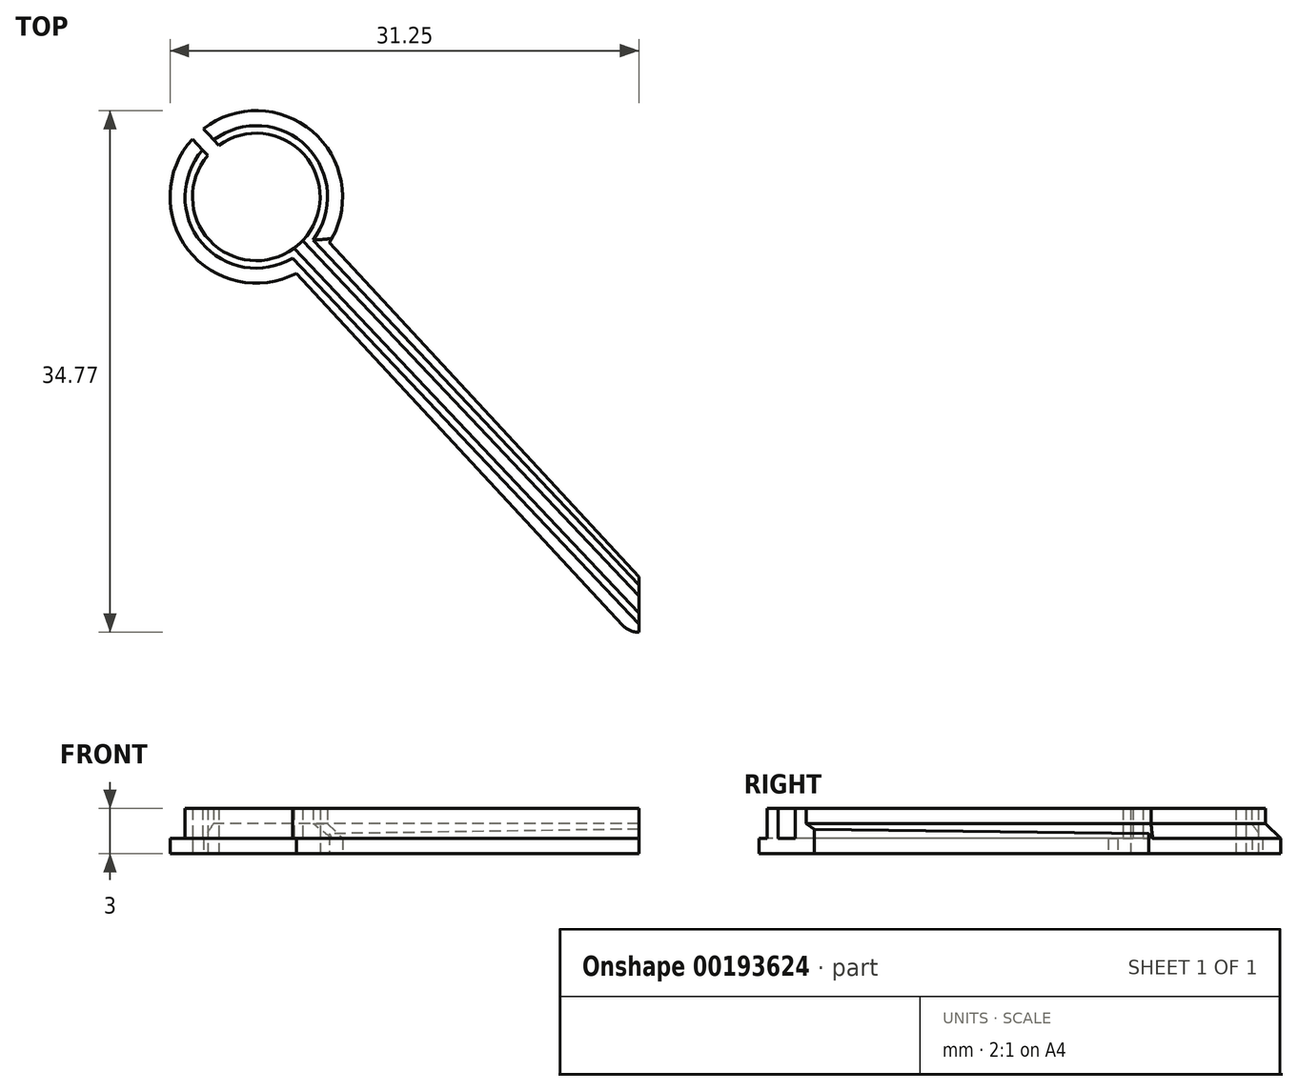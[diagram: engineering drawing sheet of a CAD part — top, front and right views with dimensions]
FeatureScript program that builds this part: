
annotation { "Feature Type Name" : "Feature", "Feature Type Description" : "" }
export const myFeature = defineFeature(function(context is Context, id is Id, definition is map)
    precondition{}
    {
        {
            var Q0;
            Q0=qCreatedBy(makeId("Top.planeOp"),FACE);
            var sketch = newSketch(context, id + "F0", { "sketchPlane" : qUnion([Q0])});
            skCircle(sketch, "E0", {"center": v(-37, 37) * mm, "radius": 4.25 * mm});
            skCircle(sketch, "E1", {"center": v(-9, 21) * mm, "radius": 1.7 * mm});
            skLineSegment(sketch, "E2", {"start": v(-51.17, 0) * mm, "end": v(69.36, 0) * mm, "construction": true});
            skLineSegment(sketch, "E3", {"start": v(0, -19.4) * mm, "end": v(0, 36.88) * mm, "construction": true});
            skCircle(sketch, "E4.MirrorC", {"center": v(37, 37) * mm, "radius": 4.25 * mm});
            skCircle(sketch, "E5.MirrorC", {"center": v(37, -37) * mm, "radius": 4.25 * mm});
            skCircle(sketch, "E6.MirrorC", {"center": v(-37, -37) * mm, "radius": 4.25 * mm});
            skCircle(sketch, "E7.MirrorC", {"center": v(-9, -21) * mm, "radius": 1.7 * mm});
            skCircle(sketch, "E8.MirrorC", {"center": v(9, -21) * mm, "radius": 1.7 * mm});
            skCircle(sketch, "E9.MirrorC", {"center": v(9, 21) * mm, "radius": 1.7 * mm});
            skCircle(sketch, "E10", {"center": v(-9, 21) * mm, "radius": 2.5 * mm});
            skCircle(sketch, "E11.MirrorC", {"center": v(9, 21) * mm, "radius": 2.5 * mm});
            skCircle(sketch, "E12.MirrorC", {"center": v(-9, -21) * mm, "radius": 2.5 * mm});
            skCircle(sketch, "E13.MirrorC", {"center": v(9, -21) * mm, "radius": 2.5 * mm});
            skCircle(sketch, "E14", {"center": v(-37, 37) * mm, "radius": 5.75 * mm});
            skCircle(sketch, "E15.MirrorC", {"center": v(37, 37) * mm, "radius": 5.75 * mm});
            skCircle(sketch, "E16.MirrorC", {"center": v(-37, -37) * mm, "radius": 5.75 * mm});
            skCircle(sketch, "E17.MirrorC", {"center": v(37, -37) * mm, "radius": 5.75 * mm});
            skLineSegment(sketch, "E18", {"start": v(-11.5, 18) * mm, "end": v(-8.5, 18) * mm});
            skLineSegment(sketch, "E19", {"start": v(-11.5, 15) * mm, "end": v(-11.5, 18) * mm});
            skPoint(sketch, "E20", {"position": v(0, 0) * mm});
            skLineSegment(sketch, "E21", {"start": v(-11.5, 15) * mm, "end": v(-8.5, 15) * mm});
            skLineSegment(sketch, "E22", {"start": v(-8.5, 15) * mm, "end": v(-8.5, 18) * mm});
            skLineSegment(sketch, "E23", {"start": v(-8.5, 17) * mm, "end": v(-10.5, 17) * mm});
            skLineSegment(sketch, "E24", {"start": v(-10.5, 17) * mm, "end": v(-10.5, 15) * mm});
            skLineSegment(sketch, "E25.MirrorCS", {"start": v(11.5, 18) * mm, "end": v(8.5, 18) * mm});
            skLineSegment(sketch, "E26.MirrorCS", {"start": v(8.5, 17) * mm, "end": v(10.5, 17) * mm});
            skLineSegment(sketch, "E27.MirrorCS", {"start": v(10.5, 17) * mm, "end": v(10.5, 15) * mm});
            skLineSegment(sketch, "E28.MirrorCS", {"start": v(11.5, 15) * mm, "end": v(8.5, 15) * mm});
            skLineSegment(sketch, "E29.MirrorCS", {"start": v(8.5, 15) * mm, "end": v(8.5, 18) * mm});
            skLineSegment(sketch, "E30.MirrorCS", {"start": v(11.5, 15) * mm, "end": v(11.5, 18) * mm});
            skLineSegment(sketch, "E31.MirrorCS", {"start": v(-8.5, -15) * mm, "end": v(-8.5, -18) * mm});
            skLineSegment(sketch, "E32.MirrorCS", {"start": v(-8.5, -17) * mm, "end": v(-10.5, -17) * mm});
            skLineSegment(sketch, "E33.MirrorCS", {"start": v(8.5, -17) * mm, "end": v(10.5, -17) * mm});
            skLineSegment(sketch, "E34.MirrorCS", {"start": v(8.5, -15) * mm, "end": v(8.5, -18) * mm});
            skLineSegment(sketch, "E35.MirrorCS", {"start": v(11.5, -15) * mm, "end": v(8.5, -15) * mm});
            skLineSegment(sketch, "E36.MirrorCS", {"start": v(-11.5, -15) * mm, "end": v(-8.5, -15) * mm});
            skLineSegment(sketch, "E37.MirrorCS", {"start": v(10.5, -17) * mm, "end": v(10.5, -15) * mm});
            skLineSegment(sketch, "E38.MirrorCS", {"start": v(-10.5, -17) * mm, "end": v(-10.5, -15) * mm});
            skLineSegment(sketch, "E39.MirrorCS", {"start": v(-11.5, -15) * mm, "end": v(-11.5, -18) * mm});
            skLineSegment(sketch, "E40.MirrorCS", {"start": v(11.5, -18) * mm, "end": v(8.5, -18) * mm});
            skLineSegment(sketch, "E41.MirrorCS", {"start": v(-11.5, -18) * mm, "end": v(-8.5, -18) * mm});
            skLineSegment(sketch, "E42.MirrorCS", {"start": v(11.5, -15) * mm, "end": v(11.5, -18) * mm});
            skLineSegment(sketch, "E43.bottom", {"start": v(-11.5, 23.5) * mm, "end": v(11.5, 23.5) * mm});
            skLineSegment(sketch, "E43.top", {"start": v(-11.5, -23.5) * mm, "end": v(11.5, -23.5) * mm});
            skLineSegment(sketch, "E43.left", {"start": v(-11.5, 23.5) * mm, "end": v(-11.5, -23.5) * mm});
            skLineSegment(sketch, "E43.right", {"start": v(11.5, 23.5) * mm, "end": v(11.5, -23.5) * mm});
            skLineSegment(sketch, "E44", {"start": v(-37, 37) * mm, "end": v(-11.5, 9.48) * mm, "construction": true});
            skPoint(sketch, "E45", {"position": v(-24.25, 23.24) * mm});
            skArc(sketch, "E46.0.startCap", {"start": v(-38.1, 35.98) * mm, "mid": v(-38.02, 38.1) * mm, "end": v(-35.9, 38.02) * mm});
            skArc(sketch, "E46.0.endCap", {"start": v(-10.4, 10.5) * mm, "mid": v(-10.48, 8.37) * mm, "end": v(-12.6, 8.46) * mm});
            skLineSegment(sketch, "E46.0.left", {"start": v(-35.9, 38.02) * mm, "end": v(-10.4, 10.5) * mm});
            skLineSegment(sketch, "E46.0.right", {"start": v(-38.1, 35.98) * mm, "end": v(-12.6, 8.46) * mm});
            skLineSegment(sketch, "E47", {"start": v(-37, 37) * mm, "end": v(-44.1, 44.67) * mm, "construction": true});
            skArc(sketch, "E48.0.startCap", {"start": v(-36.63, 37.34) * mm, "mid": v(-36.66, 36.63) * mm, "end": v(-37.37, 36.66) * mm});
            skArc(sketch, "E48.0.endCap", {"start": v(-44.47, 44.33) * mm, "mid": v(-44.45, 45.04) * mm, "end": v(-43.74, 45.01) * mm});
            skLineSegment(sketch, "E48.0.left", {"start": v(-37.37, 36.66) * mm, "end": v(-44.47, 44.33) * mm});
            skLineSegment(sketch, "E48.0.right", {"start": v(-36.63, 37.34) * mm, "end": v(-43.74, 45.01) * mm});
            skSolve(sketch);
        }
        {
            var Q0;
            {var subQ0=sQuery(id+"F0.wireOp",EDGE,"E48.0.left");var subQ1=sQuery(id+"F0.wireOp",EDGE,"E0");var subQ2=makeQuery(id+"F0.imprint","INTERSECT",VERTEX,{"derivedFrom":[subQ1,subQ0]});Q0=makeQuery(id+"F0.imprint","IMPRINT",FACE,{"disambiguationData":[TD([[makeQuery(id+"F0.imprint","IMPRINT",EDGE,{"disambiguationData":[TD([[subQ2,-1.0]])],"derivedFrom":subQ1}),-1.0]])]});}
            var Q1;
            {var subQ0=sQuery(id+"F0.wireOp",EDGE,"E46.0.right");var subQ1=sQuery(id+"F0.wireOp",EDGE,"E0");var subQ2=makeQuery(id+"F0.imprint","INTERSECT",VERTEX,{"derivedFrom":[subQ1,subQ0]});Q1=makeQuery(id+"F0.imprint","IMPRINT",FACE,{"disambiguationData":[TD([[makeQuery(id+"F0.imprint","IMPRINT",EDGE,{"disambiguationData":[TD([[subQ2,-1.0]])],"derivedFrom":subQ1}),-1.0]])]});}
            var Q2;
            {var subQ0=sQuery(id+"F0.wireOp",EDGE,"E48.0.right");var subQ1=sQuery(id+"F0.wireOp",EDGE,"E0");var subQ2=makeQuery(id+"F0.imprint","INTERSECT",VERTEX,{"derivedFrom":[subQ1,subQ0]});Q2=makeQuery(id+"F0.imprint","IMPRINT",FACE,{"disambiguationData":[TD([[makeQuery(id+"F0.imprint","IMPRINT",EDGE,{"disambiguationData":[TD([[subQ2,1.0]])],"derivedFrom":subQ1}),-1.0]])]});}
            var Q3;
            {var subQ1=sQuery(id+"F0.wireOp",EDGE,"E14");var subQ5=sQuery(id+"F0.wireOp",EDGE,"E46.0.right");var subQ9=makeQuery(id+"F0.imprint","INTERSECT",VERTEX,{"derivedFrom":[subQ1,subQ5]});Q3=makeQuery(id+"F0.imprint","IMPRINT",FACE,{"disambiguationData":[TD([[makeQuery(id+"F0.imprint","IMPRINT",EDGE,{"disambiguationData":[TD([[subQ9,-1.0]])],"derivedFrom":subQ1}),-1.0]])]});}
            extrude(context, id + "F1", {"entities" : qUnion([Q0, Q1, Q2, Q3]), "depth" : 1 * mm});
        }
        {
            var Q0;
            Q0=makeQuery(id+"F1.opExtrude","CAP_FACE",FACE,{"disambiguationData":[OSD([sQuery(id+"F0.wireOp",EDGE,"E0"),sQuery(id+"F0.wireOp",EDGE,"E14"),sQuery(id+"F0.wireOp",EDGE,"E43.left"),sQuery(id+"F0.wireOp",EDGE,"E46.0.endCap"),sQuery(id+"F0.wireOp",EDGE,"E46.0.left"),sQuery(id+"F0.wireOp",EDGE,"E46.0.right"),sQuery(id+"F0.wireOp",EDGE,"E48.0.left"),sQuery(id+"F0.wireOp",EDGE,"E48.0.right")])],"isStart":false});
            var sketch = newSketch(context, id + "F2", { "sketchPlane" : qUnion([Q0])});
            skCircle(sketch, "E49", {"center": v(-37, 37) * mm, "radius": 4.75 * mm});
            skLineSegment(sketch, "E50", {"start": v(-28.9, 26.04) * mm, "end": v(-26.7, 28.08) * mm, "construction": true});
            skPoint(sketch, "E51", {"position": v(-27.8, 27.06) * mm});
            skLineSegment(sketch, "E52", {"start": v(-33.84, 33.46) * mm, "end": v(-11.5, 9.83) * mm, "construction": true});
            skLineSegment(sketch, "E53", {"start": v(-34.15, 33.2) * mm, "end": v(-11.5, 9.25) * mm});
            skLineSegment(sketch, "E54", {"start": v(-33.55, 33.73) * mm, "end": v(-11.5, 10.41) * mm});
            skLineSegment(sketch, "E55", {"start": v(-30.14, 28.96) * mm, "end": v(-29.56, 29.51) * mm, "construction": true});
            skPoint(sketch, "E56", {"position": v(-29.85, 29.24) * mm});
            skArc(sketch, "E57.0", {"start": v(-40.24, 39.76) * mm, "mid": v(-34.11, 33.88) * mm, "end": v(-39.5, 40.44) * mm});
            skLineSegment(sketch, "E58", {"start": v(-40.24, 39.76) * mm, "end": v(-40.58, 40.13) * mm});
            skLineSegment(sketch, "E59", {"start": v(-39.5, 40.44) * mm, "end": v(-39.84, 40.8) * mm});
            skLineSegment(sketch, "E60", {"start": v(-34.57, 32.92) * mm, "end": v(-11.5, 8.52) * mm});
            skLineSegment(sketch, "E61", {"start": v(-33.22, 34.12) * mm, "end": v(-11.5, 11.14) * mm});
            skLineSegment(sketch, "E62", {"start": v(-34.15, 33.2) * mm, "end": v(-34.57, 33.65) * mm});
            skLineSegment(sketch, "E63", {"start": v(-33.55, 33.73) * mm, "end": v(-33.9, 34.1) * mm});
            skSolve(sketch);
        }
        {
            var Q0;
            {var subQ0=sQuery(id+"F2.wireOp",EDGE,"E53");Q0=makeQuery(id+"F2.imprint","IMPRINT",FACE,{"disambiguationData":[TD([[makeQuery(id+"F2.imprint","IMPRINT",EDGE,{"derivedFrom":subQ0}),-1.0]])]});}
            var Q1;
            {var subQ0=sQuery(id+"F2.wireOp",EDGE,"E54");Q1=makeQuery(id+"F2.imprint","IMPRINT",FACE,{"disambiguationData":[TD([[makeQuery(id+"F2.imprint","IMPRINT",EDGE,{"derivedFrom":subQ0}),1.0]])]});}
            var Q2;
            {var subQ0=sQuery(id+"F2.wireOp",EDGE,"E58");Q2=makeQuery(id+"F2.imprint","IMPRINT",FACE,{"disambiguationData":[TD([[makeQuery(id+"F2.imprint","IMPRINT",EDGE,{"derivedFrom":subQ0}),1.0]])]});}
            var Q3;
            {var subQ0=sQuery(id+"F2.wireOp",EDGE,"E59");Q3=makeQuery(id+"F2.imprint","IMPRINT",FACE,{"disambiguationData":[TD([[makeQuery(id+"F2.imprint","IMPRINT",EDGE,{"derivedFrom":subQ0}),-1.0]])]});}
            extrude(context, id + "F3", {"entities" : qUnion([Q0, Q1, Q2, Q3]), "operationType" : NewBodyOperationType.ADD, "depth" : 2 * mm});
        }
        {
            var Q0;
            Q0=makeQuery(id+"F3.opExtrude","CAP_EDGE",EDGE,{"disambiguationData":[OSD([sQuery(id+"F2.wireOp",EDGE,"E60")])],"isStart":true});
            var Q1;
            Q1=makeQuery(id+"F3.opExtrude","CAP_EDGE",EDGE,{"disambiguationData":[OSD([sQuery(id+"F2.wireOp",EDGE,"E61")])],"isStart":true});
            var Q2;
            {var subQ0=sQuery(id+"F2.wireOp",EDGE,"E49");Q2=makeQuery(id+"F3.opExtrude","CAP_EDGE",EDGE,{"disambiguationData":[OSD([subQ0]),TDD([makeQuery(id+"F2.imprint","IMPRINT",EDGE,{"disambiguationData":[TD([[makeQuery(id+"F2.imprint","INTERSECT",VERTEX,{"derivedFrom":[subQ0,sQuery(id+"F2.wireOp",EDGE,"E60")]}),1.0]])],"derivedFrom":subQ0})])],"isStart":true});}
            var Q3;
            {var subQ0=sQuery(id+"F2.wireOp",EDGE,"E49");Q3=makeQuery(id+"F3.opExtrude","CAP_EDGE",EDGE,{"disambiguationData":[OSD([subQ0]),TDD([makeQuery(id+"F2.imprint","IMPRINT",EDGE,{"disambiguationData":[TD([[makeQuery(id+"F2.imprint","INTERSECT",VERTEX,{"derivedFrom":[subQ0,sQuery(id+"F2.wireOp",EDGE,"E61")]}),-1.0]])],"derivedFrom":subQ0})])],"isStart":true});}
            chamfer(context, id + "F4", {"entities" : qUnion([Q0, Q1, Q2, Q3]), "width" : 1 * mm, "tangentPropagation" : true});
        }
    });
